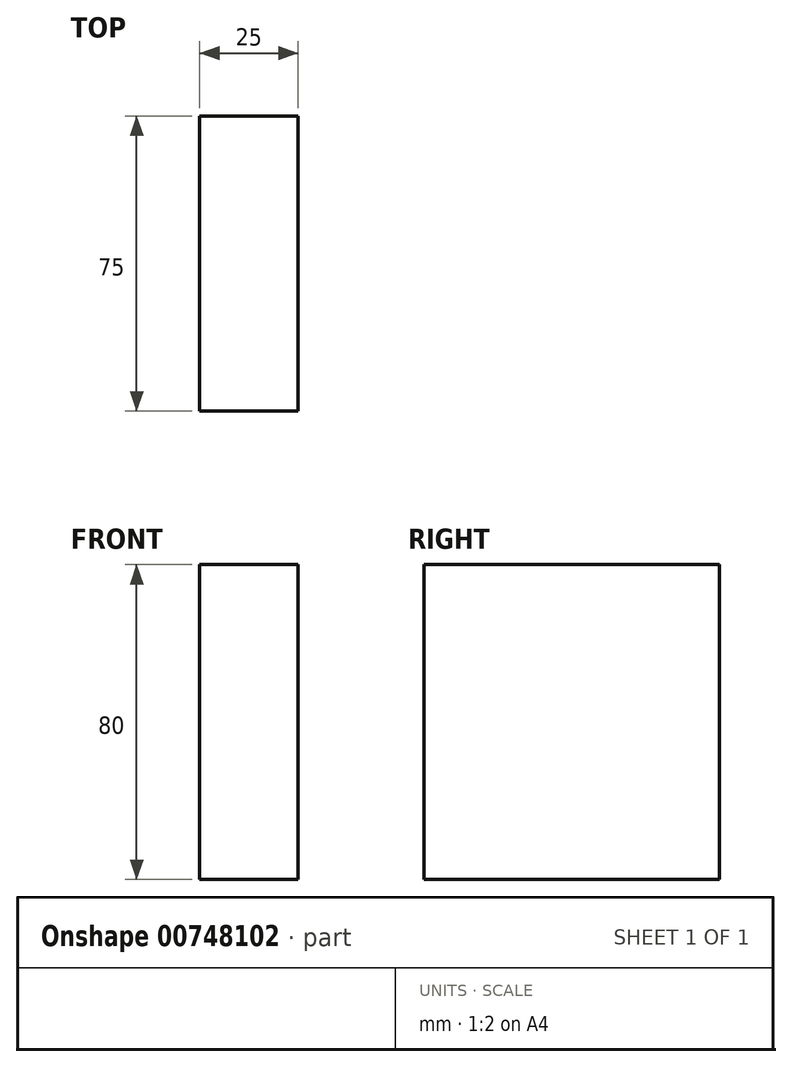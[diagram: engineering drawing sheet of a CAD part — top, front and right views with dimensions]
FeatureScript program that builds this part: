
annotation { "Feature Type Name" : "Feature", "Feature Type Description" : "" }
export const myFeature = defineFeature(function(context is Context, id is Id, definition is map)
    precondition{}
    {
        {
            var Q0;
            Q0=qCreatedBy(makeId("Right.planeOp"),FACE);
            var sketch = newSketch(context, id + "F0", { "sketchPlane" : qUnion([Q0])});
            skLineSegment(sketch, "E0.bottom", {"start": v(-89.74, 30.53) * mm, "end": v(-14.74, 30.53) * mm});
            skLineSegment(sketch, "E0.top", {"start": v(-89.74, -49.47) * mm, "end": v(-14.74, -49.47) * mm});
            skLineSegment(sketch, "E0.left", {"start": v(-89.74, 30.53) * mm, "end": v(-89.74, -49.47) * mm});
            skLineSegment(sketch, "E0.right", {"start": v(-14.74, 30.53) * mm, "end": v(-14.74, -49.47) * mm});
            skSolve(sketch);
        }
        {
            var Q0;
            Q0=makeQuery(id+"F0.imprint","IMPRINT",FACE,{"disambiguationData":[TD([[makeQuery(id+"F0.imprint","IMPRINT",EDGE,{"derivedFrom":sQuery(id+"F0.wireOp",EDGE,"E0.bottom")}),-1.0]])]});
            extrude(context, id + "F1", {"entities" : qUnion([Q0]), "depth" : 25 * mm, "offsetDistance" : 25 * mm});
        }
        {
            var Q0;
            Q0=makeQuery(id+"F0.imprint","IMPRINT",FACE,{"disambiguationData":[TD([[makeQuery(id+"F0.imprint","IMPRINT",EDGE,{"derivedFrom":sQuery(id+"F0.wireOp",EDGE,"E0.bottom")}),-1.0]])]});
            extrude(context, id + "F2", {"entities" : qUnion([Q0]), "operationType" : NewBodyOperationType.ADD, "depth" : 25 * mm, "offsetDistance" : 25 * mm});
        }
        {
            var Q0;
            Q0=makeQuery(id+"F0.imprint","IMPRINT",FACE,{"disambiguationData":[TD([[makeQuery(id+"F0.imprint","IMPRINT",EDGE,{"derivedFrom":sQuery(id+"F0.wireOp",EDGE,"E0.bottom")}),-1.0]])]});
            extrude(context, id + "F3", {"entities" : qUnion([Q0]), "operationType" : NewBodyOperationType.ADD, "depth" : 25 * mm, "offsetDistance" : 25 * mm});
        }
    });
